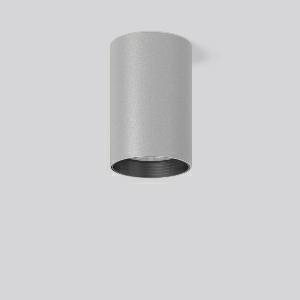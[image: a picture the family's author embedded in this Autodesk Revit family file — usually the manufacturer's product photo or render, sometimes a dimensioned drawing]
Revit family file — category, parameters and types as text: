
# Revit family: heledon_maxi_a_931220_004_76_ed56
name_source: partatom
category: Lighting Fixtures
units: mm (PartAtom-declared; Revit-internal decimal feet)

## family parameters
Cut with Voids When Loaded = No
Host = Face
Light Source = No
Part Type = Normal
Room Calculation Point = No
Round Connector Dimension = Use Diameter
Shared = No

## types (1)
- HELEDON maxi A (1 x LED Modul 930, 2850 lm, 3000)
    Apparent Load = 25 VA
    Approval mark = CE
    CIE Flux Codes = 97 100 100 100 100
    Color Rendering = 90
    Color Temperature = 3000
    Default Elevation = 1800 mm
    Description = Series: HELEDON maxi
Cylindrical surface-mounted downlight. Housing: die-cast aluminium, powder-coated. Internal ceiling frame polycarbonate with bayonet mounting. Black plastic ring and recessed LED to prevent glare from the side. Optical assembly with lens made of plastic (polycarbonate) for the best homogeneous light distribution - can be changed without tools. Best colour rendering index Ra>90. Suitable for Ceiling mounting. Easy installation with a separate ceiling frame with bayonet mounting and plug connection. Driver integrated. Connected via plug-in connector. High quality converter without flickering and stroboscopic effect. The following accessories can be mounted without use of tools: interchangeable lenses, decorative glasses, honeycomb louvre, clear and frosted diffusers, white interchangeable plastic ring. 
Colour: silver
Diameter: 123 mm
Height: 183 mm
Lamp: LED
Socket: without socket
Colour temperature: 3000K
Colour rendering index (CRI): 92
System power: 25 W
Rated luminous flux: 2850 lm
Luminous efficiency: 114 lm/W
Control gear: Converter, dimmable, DALI
Protection class: I
Type of protection: IP 20
    Height = 183 mm
    Lamp = 1 x LED Modul 930
    Lamp Light Flux = 2850 lm
    Lamp count = 1
    Length = 123 mm
    Lifetime = 50000 h
    Luminous efficacy = 114 lm/W
    Manufacturer = RZB
    ModVariant = No
    Model = 931220.004.76
    Mounting Place = Ceiling
    Mounting Type = Surface mounted
    Number of Poles = 1
    OnlyDefault = Yes
    Power Factor = 1
    Product Name = HELEDON maxi A
    Product group = Surface mounted downlights
    ProductGroupID = 302
    Protection Class = Protection class I
    Protection Degree = IP 20
    RLX_Detail_Level = 1
    RLX_Emergency_Light_Flux = 0 lm
    RLX_Emergency_Type = 0
    RLX_Emergency_Type_DB = No
    RlxData = <blob elided: 98717 chars, md5=df5ec828>
    Socket = socket
    Standby Power = 0 W
    System Light Flux = 2850 lm
    System Power = 25 W
    Type Comments = Product without accessories
    Type Image = 931193.004.jpg
    URL = http://relux.com
    VarID = ---
    Voltage = 230 V
    Voltage Range = 220-240 V
    Weight = 0.00 kg
    Width = 0 mm  [stored 0 ft]

note: [stored X ft] marks values corroborated as IEEE doubles in the binary element streams (Revit-internal decimal feet)

## geometry (parser evidence)
native form markers: Blend x4, Sweep x11
no freeform markers — native parametric forms only
